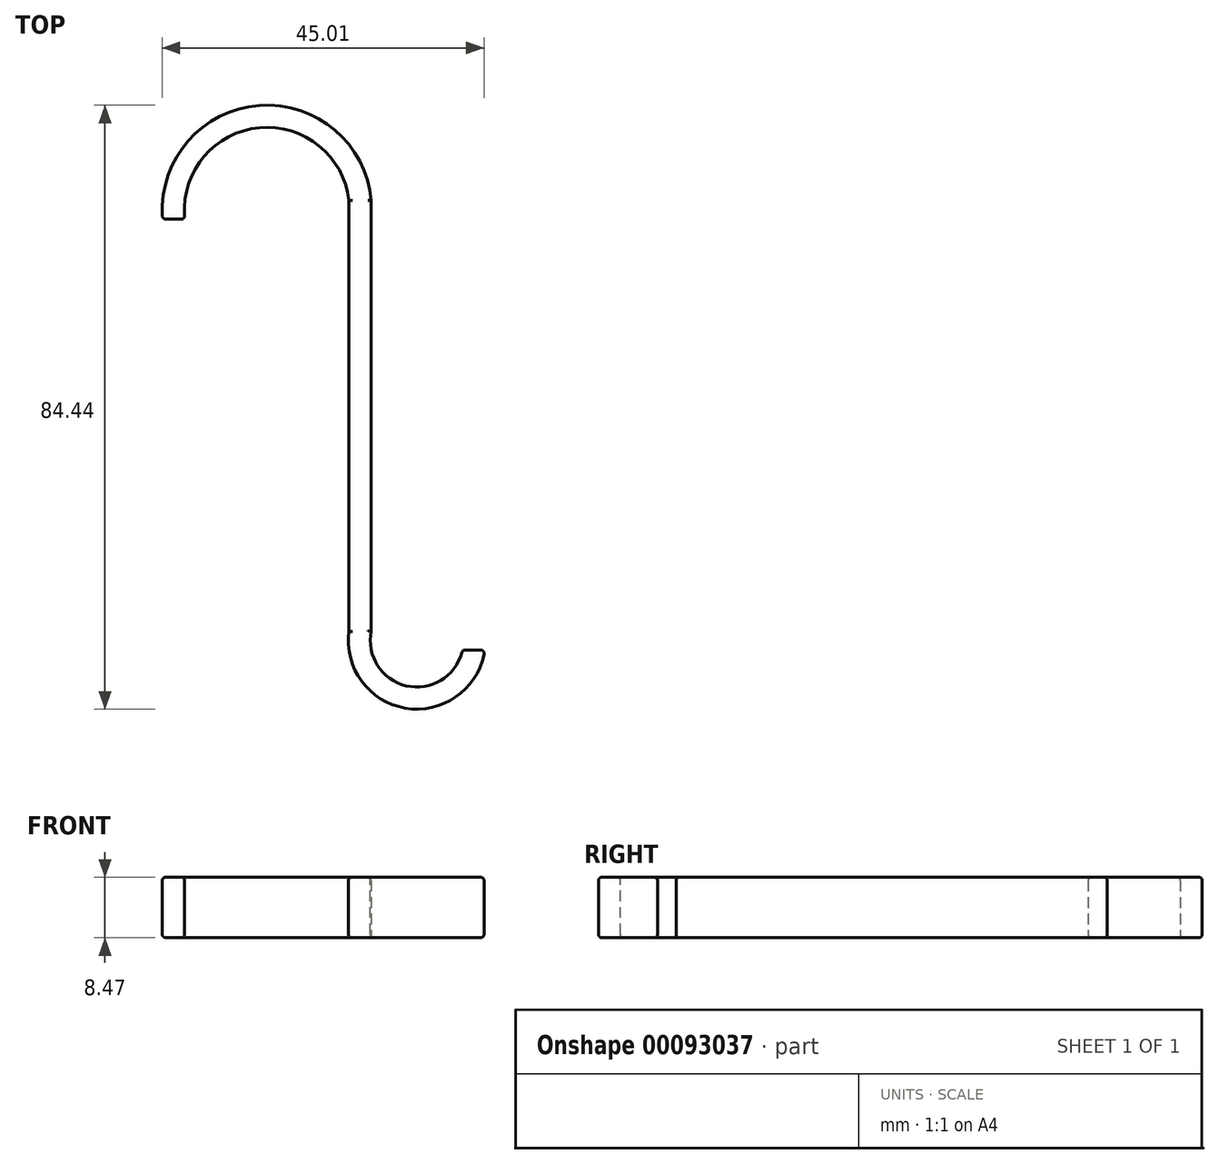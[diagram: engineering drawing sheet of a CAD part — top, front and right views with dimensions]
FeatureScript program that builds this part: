
annotation { "Feature Type Name" : "Feature", "Feature Type Description" : "" }
export const myFeature = defineFeature(function(context is Context, id is Id, definition is map)
    precondition{}
    {
        {
            var Q0;
            Q0=qCreatedBy(makeId("Top.planeOp"),FACE);
            var sketch = newSketch(context, id + "F0", { "sketchPlane" : qUnion([Q0])});
            skLineSegment(sketch, "E0", {"start": v(0, 31.31) * mm, "end": v(0, -28.9) * mm});
            skArc(sketch, "E1", {"start": v(0, 31.31) * mm, "mid": v(-10.2, 41.51) * mm, "end": v(-20.4, 31.31) * mm});
            skArc(sketch, "E2", {"start": v(0, -28.9) * mm, "mid": v(10.76, -39.65) * mm, "end": v(21.52, -28.9) * mm});
            skSolve(sketch);
        }
        {
            var Q0;
            Q0=qCreatedBy(makeId("Front.planeOp"),FACE);
            var sketch = newSketch(context, id + "F1", { "sketchPlane" : qUnion([Q0])});
            skLineSegment(sketch, "E3.bottom", {"start": v(-23.4, -4.05) * mm, "end": v(-20.4, -4.05) * mm});
            skLineSegment(sketch, "E3.top", {"start": v(-23.4, 3.95) * mm, "end": v(-20.4, 3.95) * mm});
            skLineSegment(sketch, "E3.left", {"start": v(-23.4, -4.05) * mm, "end": v(-23.4, 3.95) * mm});
            skLineSegment(sketch, "E3.right", {"start": v(-20.4, -4.05) * mm, "end": v(-20.4, 3.95) * mm});
            skSolve(sketch);
        }
        {
            var Q0;
            Q0=qCreatedBy(makeId("Front.planeOp"),FACE);
            cPlane(context, id + "F2", {"entities" : qUnion([Q0]), "cplaneType" : CPlaneType.OFFSET, "offset" : 30 * mm, "oppositeDirection" : true, "width" : 150 * mm, "height" : 150 * mm});
        }
        {
            var Q0;
            Q0=qCreatedBy(id+"F2.planeOp",FACE);
            var sketch = newSketch(context, id + "F3", { "sketchPlane" : qUnion([Q0])});
            skLineSegment(sketch, "E4.bottom", {"start": v(-24.79, 4.3) * mm, "end": v(-21.66, 4.3) * mm});
            skLineSegment(sketch, "E4.top", {"start": v(-24.79, -4.17) * mm, "end": v(-21.66, -4.17) * mm});
            skLineSegment(sketch, "E4.left", {"start": v(-24.79, 4.3) * mm, "end": v(-24.79, -4.17) * mm});
            skLineSegment(sketch, "E4.right", {"start": v(-21.66, 4.3) * mm, "end": v(-21.66, -4.17) * mm});
            skSolve(sketch);
        }
        {
            var Q0;
            Q0=makeQuery(id+"F3.imprint","IMPRINT",FACE,{"disambiguationData":[TD([[makeQuery(id+"F3.imprint","IMPRINT",EDGE,{"derivedFrom":sQuery(id+"F3.wireOp",EDGE,"E4.bottom")}),-1.0]])]});
            var Q1;
            Q1=sQuery(id+"F0.wireOp",EDGE,"E1");
            sweep(context, id + "F4", {"profiles" : qUnion([Q0]), "path" : qUnion([Q1])});
        }
        {
            var Q0;
            Q0=makeQuery(id+"F4.opSweep","CAP_FACE",FACE,{"disambiguationData":[OSD([sQuery(id+"F0.wireOp",VERTEX,"E1.start"),sQuery(id+"F3.wireOp",EDGE,"E4.bottom"),sQuery(id+"F3.wireOp",EDGE,"E4.top"),sQuery(id+"F3.wireOp",EDGE,"E4.left"),sQuery(id+"F3.wireOp",EDGE,"E4.right")])],"isStart":false});
            var Q1;
            Q1=sQuery(id+"F0.wireOp",EDGE,"E0");
            sweep(context, id + "F5", {"operationType" : NewBodyOperationType.ADD, "profiles" : qUnion([Q0]), "path" : qUnion([Q1])});
        }
        {
            var Q0;
            Q0=makeQuery(id+"F5.opSweep","CAP_FACE",FACE,{"disambiguationData":[OSD([sQuery(id+"F0.wireOp",VERTEX,"E0.end"),sQuery(id+"F0.wireOp",VERTEX,"E1.start"),sQuery(id+"F3.wireOp",EDGE,"E4.bottom"),sQuery(id+"F3.wireOp",EDGE,"E4.top"),sQuery(id+"F3.wireOp",EDGE,"E4.left"),sQuery(id+"F3.wireOp",EDGE,"E4.right")])],"isStart":false});
            var Q1;
            Q1=sQuery(id+"F0.wireOp",EDGE,"E2");
            sweep(context, id + "F6", {"operationType" : NewBodyOperationType.ADD, "profiles" : qUnion([Q0]), "path" : qUnion([Q1])});
        }
        {
            var Q0;
            {var subQ0=sQuery(id+"F3.wireOp",EDGE,"E4.bottom");var subQ1=sQuery(id+"F0.wireOp",VERTEX,"E1.start");Q0=makeQuery(id+"F6.boolean.opBoolean","MERGE",FACE,{"derivedFrom":[makeQuery(id+"F5.boolean.opBoolean","MERGE",FACE,{"derivedFrom":[makeQuery(id+"F4.opSweep","SWEPT_FACE",FACE,{"disambiguationData":[OSD([sQuery(id+"F0.wireOp",EDGE,"E1"),subQ0])]}),makeQuery(id+"F5.opSweep","SWEPT_FACE",FACE,{"disambiguationData":[OSD([subQ1,sQuery(id+"F0.wireOp",EDGE,"E0"),subQ0])]})]}),makeQuery(id+"F6.opSweep","SWEPT_FACE",FACE,{"disambiguationData":[OSD([sQuery(id+"F0.wireOp",VERTEX,"E0.end"),subQ1,sQuery(id+"F0.wireOp",EDGE,"E2"),subQ0])]})]});}
            var Q1;
            {var subQ0=sQuery(id+"F3.wireOp",EDGE,"E4.top");var subQ1=sQuery(id+"F0.wireOp",VERTEX,"E1.start");Q1=makeQuery(id+"F6.boolean.opBoolean","MERGE",FACE,{"derivedFrom":[makeQuery(id+"F5.boolean.opBoolean","MERGE",FACE,{"derivedFrom":[makeQuery(id+"F4.opSweep","SWEPT_FACE",FACE,{"disambiguationData":[OSD([sQuery(id+"F0.wireOp",EDGE,"E1"),subQ0])]}),makeQuery(id+"F5.opSweep","SWEPT_FACE",FACE,{"disambiguationData":[OSD([subQ1,sQuery(id+"F0.wireOp",EDGE,"E0"),subQ0])]})]}),makeQuery(id+"F6.opSweep","SWEPT_FACE",FACE,{"disambiguationData":[OSD([sQuery(id+"F0.wireOp",VERTEX,"E0.end"),subQ1,sQuery(id+"F0.wireOp",EDGE,"E2"),subQ0])]})]});}
            var Q2;
            Q2=makeQuery(id+"F4.opSweep","CAP_FACE",FACE,{"disambiguationData":[OSD([sQuery(id+"F0.wireOp",VERTEX,"E1.end"),sQuery(id+"F3.wireOp",EDGE,"E4.bottom"),sQuery(id+"F3.wireOp",EDGE,"E4.top"),sQuery(id+"F3.wireOp",EDGE,"E4.left"),sQuery(id+"F3.wireOp",EDGE,"E4.right")])],"isStart":true});
            var Q3;
            Q3=makeQuery(id+"F6.opSweep","CAP_FACE",FACE,{"disambiguationData":[OSD([sQuery(id+"F0.wireOp",VERTEX,"E0.end"),sQuery(id+"F0.wireOp",VERTEX,"E1.start"),sQuery(id+"F0.wireOp",VERTEX,"E2.end"),sQuery(id+"F3.wireOp",EDGE,"E4.bottom"),sQuery(id+"F3.wireOp",EDGE,"E4.top"),sQuery(id+"F3.wireOp",EDGE,"E4.left"),sQuery(id+"F3.wireOp",EDGE,"E4.right")])],"isStart":false});
            fillet(context, id + "F7", {"entities" : qUnion([Q0, Q1, Q2, Q3]), "radius" : 0.5 * mm, "tangentPropagation" : true, "allowEdgeOverflow" : false});
        }
    });
